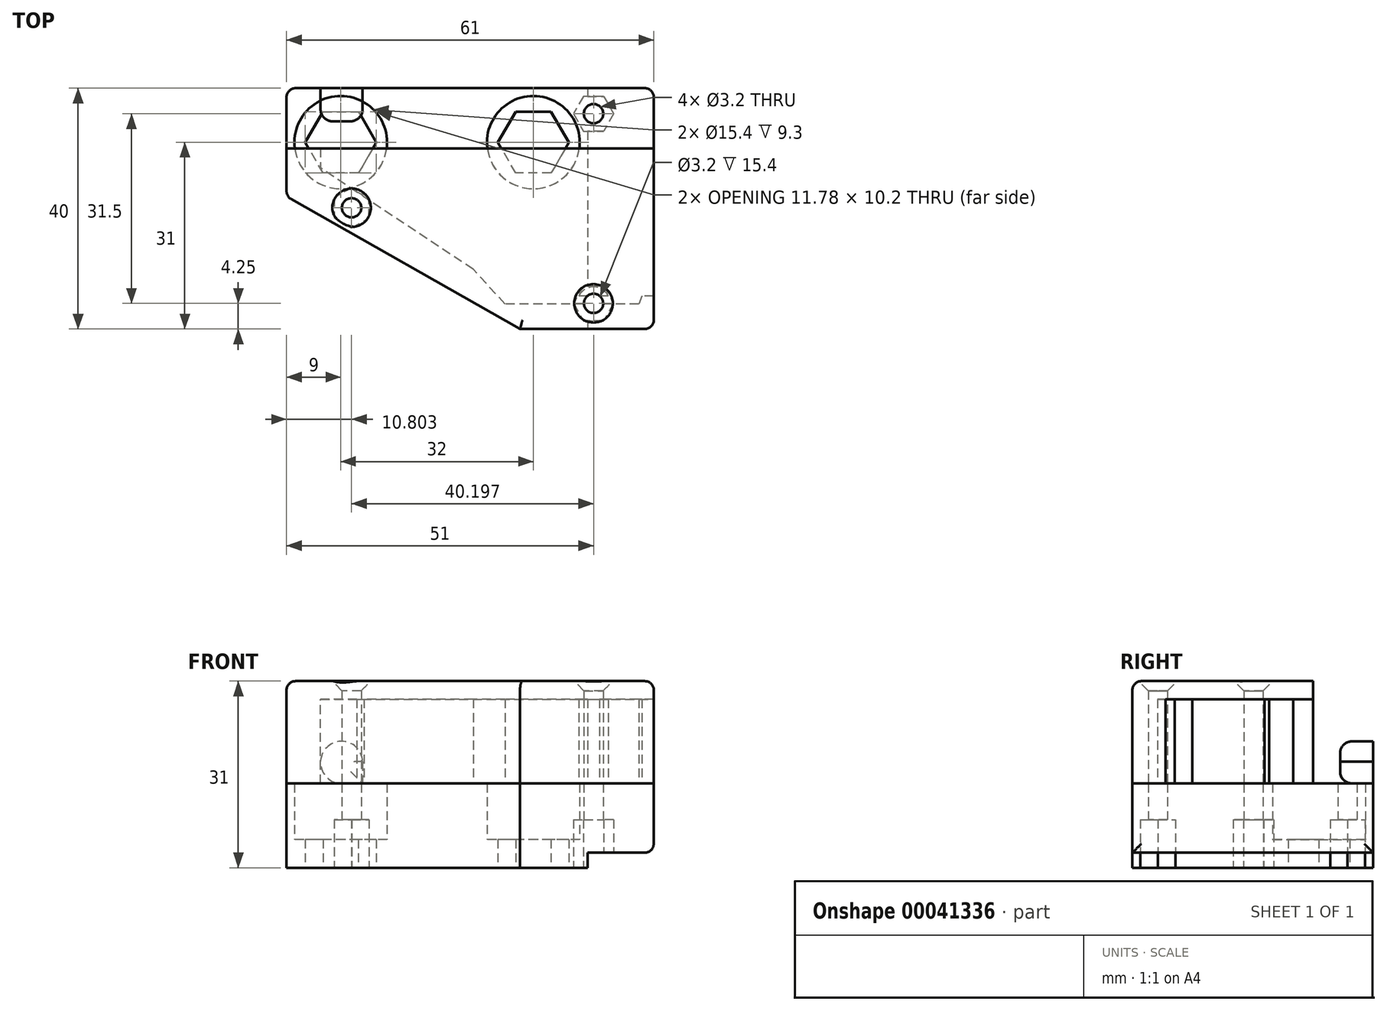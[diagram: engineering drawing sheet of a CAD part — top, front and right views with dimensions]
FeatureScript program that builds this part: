
annotation { "Feature Type Name" : "Feature", "Feature Type Description" : "" }
export const myFeature = defineFeature(function(context is Context, id is Id, definition is map)
    precondition{}
    {
        {
            var Q0;
            Q0=qCreatedBy(makeId("Top.planeOp"),FACE);
            var sketch = newSketch(context, id + "F0", { "sketchPlane" : qUnion([Q0])});
            skLineSegment(sketch, "E0", {"start": v(0, 0) * mm, "end": v(16, 0) * mm, "construction": true});
            skLineSegment(sketch, "E1", {"start": v(0, 0) * mm, "end": v(-16, 0) * mm, "construction": true});
            skCircle(sketch, "E2.cCircle", {"center": v(-16, 0) * mm, "radius": 5.1 * mm, "construction": true});
            skLineSegment(sketch, "E2.0", {"start": v(-13.06, -5.1) * mm, "end": v(-18.94, -5.1) * mm});
            skLineSegment(sketch, "E2.1", {"start": v(-18.94, -5.1) * mm, "end": v(-21.89, 0) * mm});
            skLineSegment(sketch, "E2.2", {"start": v(-21.89, 0) * mm, "end": v(-18.94, 5.1) * mm});
            skLineSegment(sketch, "E2.3", {"start": v(-18.94, 5.1) * mm, "end": v(-13.06, 5.1) * mm});
            skLineSegment(sketch, "E2.4", {"start": v(-13.06, 5.1) * mm, "end": v(-10.11, 0) * mm});
            skLineSegment(sketch, "E2.5", {"start": v(-10.11, 0) * mm, "end": v(-13.06, -5.1) * mm});
            skPoint(sketch, "E2.0.midPoint", {"position": v(-16, -5.1) * mm});
            skCircle(sketch, "E3.cCircle", {"center": v(16, 0) * mm, "radius": 5.1 * mm, "construction": true});
            skLineSegment(sketch, "E3.0", {"start": v(18.94, -5.1) * mm, "end": v(13.06, -5.1) * mm});
            skLineSegment(sketch, "E3.1", {"start": v(13.06, -5.1) * mm, "end": v(10.11, 0) * mm});
            skLineSegment(sketch, "E3.2", {"start": v(10.11, 0) * mm, "end": v(13.06, 5.1) * mm});
            skLineSegment(sketch, "E3.3", {"start": v(13.06, 5.1) * mm, "end": v(18.94, 5.1) * mm});
            skLineSegment(sketch, "E3.4", {"start": v(18.94, 5.1) * mm, "end": v(21.89, 0) * mm});
            skLineSegment(sketch, "E3.5", {"start": v(21.89, 0) * mm, "end": v(18.94, -5.1) * mm});
            skPoint(sketch, "E3.0.midPoint", {"position": v(16, -5.1) * mm});
            skLineSegment(sketch, "E4.rect.bottom", {"start": v(25, 9) * mm, "end": v(-25, 9) * mm});
            skLineSegment(sketch, "E4.rect.top", {"start": v(25, -9) * mm, "end": v(-25, -9) * mm});
            skLineSegment(sketch, "E4.rect.left", {"start": v(25, 9) * mm, "end": v(25, -9) * mm});
            skLineSegment(sketch, "E4.rect.right", {"start": v(-25, 9) * mm, "end": v(-25, -9) * mm});
            skPoint(sketch, "E4.rect.middle", {"position": v(0, 0) * mm});
            skCircle(sketch, "E5", {"center": v(16, 0) * mm, "radius": 7.7 * mm});
            skCircle(sketch, "E6", {"center": v(-16, 0) * mm, "radius": 7.7 * mm});
            skLineSegment(sketch, "E7", {"start": v(25, -9) * mm, "end": v(25, -31) * mm});
            skLineSegment(sketch, "E8", {"start": v(25, -31) * mm, "end": v(13.8, -31) * mm});
            skLineSegment(sketch, "E9", {"start": v(13.8, -31) * mm, "end": v(-25, -9) * mm});
            skSolve(sketch);
        }
        {
            var Q0;
            Q0=makeQuery(id+"F0.imprint","IMPRINT",FACE,{"disambiguationData":[TD([[makeQuery(id+"F0.imprint","IMPRINT",EDGE,{"derivedFrom":sQuery(id+"F0.wireOp",EDGE,"E2.0")}),1.0]])]});
            var Q1;
            Q1=makeQuery(id+"F0.imprint","IMPRINT",FACE,{"disambiguationData":[TD([[makeQuery(id+"F0.imprint","IMPRINT",EDGE,{"derivedFrom":sQuery(id+"F0.wireOp",EDGE,"E4.rect.bottom")}),1.0]])]});
            var Q2;
            Q2=makeQuery(id+"F0.imprint","IMPRINT",FACE,{"disambiguationData":[TD([[makeQuery(id+"F0.imprint","IMPRINT",EDGE,{"derivedFrom":sQuery(id+"F0.wireOp",EDGE,"E3.0")}),1.0]])]});
            var Q3;
            Q3=makeQuery(id+"F0.imprint","IMPRINT",FACE,{"disambiguationData":[TD([[makeQuery(id+"F0.imprint","IMPRINT",EDGE,{"derivedFrom":sQuery(id+"F0.wireOp",EDGE,"E4.rect.top")}),1.0]])]});
            var Q4;
            Q4=makeQuery(id+"F0.imprint","IMPRINT",FACE,{"disambiguationData":[TD([[makeQuery(id+"F0.imprint","IMPRINT",EDGE,{"derivedFrom":sQuery(id+"F0.wireOp",EDGE,"9e964b0c-50f7-469d-a5f6-e5326cfa843e")}),-1.0]])]});
            var Q5;
            {var subQ3=sQuery(id+"F0.wireOp",EDGE,"6a1c6b45-991d-430d-b84b-9ebeff1134ff.2");Q5=makeQuery(id+"F0.imprint","IMPRINT",FACE,{"disambiguationData":[TD([[makeQuery(id+"F0.imprint","IMPRINT",EDGE,{"derivedFrom":subQ3}),-1.0]])]});}
            var Q6;
            Q6=makeQuery(id+"F0.imprint","IMPRINT",FACE,{"disambiguationData":[TD([[makeQuery(id+"F0.imprint","IMPRINT",EDGE,{"derivedFrom":sQuery(id+"F0.wireOp",EDGE,"208a588a-a936-4bbe-a4cd-ee4cf070bca5.5")}),-1.0]])]});
            var Q7;
            {var subQ3=sQuery(id+"F0.wireOp",EDGE,"6a1c6b45-991d-430d-b84b-9ebeff1134ff.4");Q7=makeQuery(id+"F0.imprint","IMPRINT",FACE,{"disambiguationData":[TD([[makeQuery(id+"F0.imprint","IMPRINT",EDGE,{"derivedFrom":subQ3}),-1.0]])]});}
            var Q8;
            {var subQ1=sQuery(id+"F0.wireOp",EDGE,"E4.rect.top");var subQ3=sQuery(id+"F0.wireOp",EDGE,"5dbff245-9a07-4e52-9307-8249a6cdc635.0");var subQ5=makeQuery(id+"F0.imprint","INTERSECT",VERTEX,{"derivedFrom":[subQ1,subQ3]});Q8=makeQuery(id+"F0.imprint","IMPRINT",FACE,{"disambiguationData":[TD([[makeQuery(id+"F0.imprint","IMPRINT",EDGE,{"disambiguationData":[TD([[subQ5,-1.0]])],"derivedFrom":subQ1}),-1.0]])]});}
            extrude(context, id + "F1", {"entities" : qUnion([Q0, Q1, Q2, Q3, Q4, Q5, Q6, Q7, Q8]), "depth" : 4.7 * mm});
        }
        {
            var Q0;
            Q0 = qSketchRegion(id + "F0", true);
            var Q1;
            {var subQ4=sQuery(id+"F0.wireOp",EDGE,"6a1c6b45-991d-430d-b84b-9ebeff1134ff.2");Q1=makeQuery(id+"F0.imprint","IMPRINT",FACE,{"disambiguationData":[TD([[makeQuery(id+"F0.imprint","IMPRINT",EDGE,{"derivedFrom":subQ4}),-1.0]])]});}
            var Q2;
            Q2=makeQuery(id+"F0.imprint","IMPRINT",FACE,{"disambiguationData":[TD([[makeQuery(id+"F0.imprint","IMPRINT",EDGE,{"derivedFrom":sQuery(id+"F0.wireOp",EDGE,"9e964b0c-50f7-469d-a5f6-e5326cfa843e")}),-1.0]])]});
            var Q3;
            Q3=makeQuery(id+"F0.imprint","IMPRINT",FACE,{"disambiguationData":[TD([[makeQuery(id+"F0.imprint","IMPRINT",EDGE,{"derivedFrom":sQuery(id+"F0.wireOp",EDGE,"208a588a-a936-4bbe-a4cd-ee4cf070bca5.5")}),-1.0]])]});
            extrude(context, id + "F2", {"entities" : qUnion([Q0, Q1, Q2, Q3]), "operationType" : NewBodyOperationType.ADD, "depth" : 14 * mm});
        }
        {
            var Q0;
            Q0=qCreatedBy(makeId("Top.planeOp"),FACE);
            cPlane(context, id + "F3", {"entities" : qUnion([Q0]), "cplaneType" : CPlaneType.OFFSET, "offset" : 2.5 * mm, "width" : 150 * mm, "height" : 150 * mm});
        }
        {
            var Q0;
            Q0=qCreatedBy(id+"F3.planeOp",FACE);
            var sketch = newSketch(context, id + "F4", { "sketchPlane" : qUnion([Q0])});
            skLineSegment(sketch, "E10.bottom", {"start": v(25, 9) * mm, "end": v(36, 9) * mm});
            skLineSegment(sketch, "E10.top", {"start": v(25, -31) * mm, "end": v(36, -31) * mm});
            skLineSegment(sketch, "E10.left", {"start": v(25, 9) * mm, "end": v(25, -31) * mm});
            skLineSegment(sketch, "E10.right", {"start": v(36, 9) * mm, "end": v(36, -31) * mm});
            skCircle(sketch, "E11.0", {"center": v(16, 0) * mm, "radius": 7.7 * mm});
            skSolve(sketch);
        }
        {
            var Q0;
            Q0=makeQuery(id+"F4.imprint","IMPRINT",FACE,{"disambiguationData":[TD([[makeQuery(id+"F4.imprint","IMPRINT",EDGE,{"derivedFrom":sQuery(id+"F4.wireOp",EDGE,"E10.bottom")}),-1.0]])]});
            var Q1;
            Q1=makeQuery(id+"F2.opExtrude","CAP_FACE",FACE,{"disambiguationData":[OSD([sQuery(id+"F0.wireOp",EDGE,"E4.rect.bottom"),sQuery(id+"F0.wireOp",EDGE,"E4.rect.left"),sQuery(id+"F0.wireOp",EDGE,"E4.rect.right"),sQuery(id+"F0.wireOp",EDGE,"E5"),sQuery(id+"F0.wireOp",EDGE,"E6"),sQuery(id+"F0.wireOp",EDGE,"E7"),sQuery(id+"F0.wireOp",EDGE,"ee43d7b4-246c-4edb-8c6c-6255f297e4f2")])],"isStart":false});
            extrude(context, id + "F5", {"entities" : qUnion([Q0]), "operationType" : NewBodyOperationType.ADD, "endBound" : BoundingType.UP_TO_SURFACE, "endBoundEntityFace" : qUnion([Q1]), "depth" : 25 * mm});
        }
        {
            var Q0;
            Q0=makeQuery(id+"F5.boolean.opBoolean","MERGE",FACE,{"derivedFrom":[makeQuery(id+"F2.opExtrude","CAP_FACE",FACE,{"disambiguationData":[OSD([sQuery(id+"F0.wireOp",EDGE,"E4.rect.bottom"),sQuery(id+"F0.wireOp",EDGE,"E4.rect.left"),sQuery(id+"F0.wireOp",EDGE,"E4.rect.right"),sQuery(id+"F0.wireOp",EDGE,"E5"),sQuery(id+"F0.wireOp",EDGE,"E6"),sQuery(id+"F0.wireOp",EDGE,"E7"),sQuery(id+"F0.wireOp",EDGE,"ee43d7b4-246c-4edb-8c6c-6255f297e4f2")])],"isStart":false}),makeQuery(id+"F5.opExtrude","CAP_FACE",FACE,{"disambiguationData":[OSD([sQuery(id+"F4.wireOp",EDGE,"E10.bottom"),sQuery(id+"F4.wireOp",EDGE,"E10.top"),sQuery(id+"F4.wireOp",EDGE,"E10.left"),sQuery(id+"F4.wireOp",EDGE,"E10.right")])],"isStart":false})]});
            var sketch = newSketch(context, id + "F6", { "sketchPlane" : qUnion([Q0])});
            skSolve(sketch);
        }
        {
            var Q0;
            {var subQ10=sQuery(id+"F6.wireOp",EDGE,"a482f5d8-160b-4c89-b4e5-af63eeadc495.top");Q0=makeQuery(id+"F6.imprint","IMPRINT",FACE,{"disambiguationData":[TD([[makeQuery(id+"F6.imprint","IMPRINT",EDGE,{"derivedFrom":subQ10}),1.0]])]});}
            var Q1;
            Q1=makeQuery(id+"F6.imprint","IMPRINT",FACE,{"disambiguationData":[TD([[makeQuery(id+"F6.imprint","IMPRINT",EDGE,{"derivedFrom":makeQuery(id+"F2.opExtrude","CAP_EDGE",EDGE,{"disambiguationData":[OSD([sQuery(id+"F0.wireOp",EDGE,"E6")])],"isStart":false})}),1.0]])]});
            var Q2;
            {var subQ0=sQuery(id+"F6.wireOp",EDGE,"a482f5d8-160b-4c89-b4e5-af63eeadc495.right");var subQ3=sQuery(id+"F6.wireOp",EDGE,"a482f5d8-160b-4c89-b4e5-af63eeadc495.bottom");var subQ4=makeQuery(id+"F6.imprint","INTERSECT",VERTEX,{"derivedFrom":[subQ3,subQ0]});Q2=makeQuery(id+"F6.imprint","IMPRINT",FACE,{"disambiguationData":[TD([[makeQuery(id+"F6.imprint","IMPRINT",EDGE,{"disambiguationData":[TD([[subQ4,1.0]])],"derivedFrom":subQ3}),-1.0]])]});}
            var Q3;
            {var subQ1=sQuery(id+"F6.wireOp",EDGE,"a482f5d8-160b-4c89-b4e5-af63eeadc495.right");var subQ3=sQuery(id+"F6.wireOp",EDGE,"a482f5d8-160b-4c89-b4e5-af63eeadc495.bottom");var subQ5=makeQuery(id+"F6.imprint","INTERSECT",VERTEX,{"derivedFrom":[subQ3,subQ1]});Q3=makeQuery(id+"F6.imprint","IMPRINT",FACE,{"disambiguationData":[TD([[makeQuery(id+"F6.imprint","IMPRINT",EDGE,{"disambiguationData":[TD([[subQ5,1.0]])],"derivedFrom":subQ3}),1.0]])]});}
            var Q4;
            Q4=makeQuery(id+"F6.imprint","IMPRINT",FACE,{"disambiguationData":[TD([[makeQuery(id+"F6.imprint","IMPRINT",EDGE,{"derivedFrom":makeQuery(id+"F2.opExtrude","CAP_EDGE",EDGE,{"disambiguationData":[OSD([sQuery(id+"F0.wireOp",EDGE,"E4.rect.right")])],"isStart":false})}),1.0]])]});
            var Q5;
            Q5=makeQuery(id+"F6.imprint","IMPRINT",FACE,{"disambiguationData":[TD([[makeQuery(id+"F6.imprint","IMPRINT",EDGE,{"derivedFrom":makeQuery(id+"F2.opExtrude","CAP_EDGE",EDGE,{"disambiguationData":[OSD([sQuery(id+"F0.wireOp",EDGE,"E5")])],"isStart":false})}),1.0]])]});
            extrude(context, id + "F7", {"entities" : qUnion([Q0, Q1, Q2, Q3, Q4, Q5]), "depth" : 17 * mm});
        }
        {
            var Q0;
            Q0=makeQuery(id+"F7.opExtrude","CAP_FACE",FACE,{"disambiguationData":[OSD([sQuery(id+"F0.wireOp",EDGE,"E4.rect.bottom"),sQuery(id+"F0.wireOp",EDGE,"E4.rect.right"),sQuery(id+"F0.wireOp",EDGE,"E8"),sQuery(id+"F0.wireOp",EDGE,"E9"),sQuery(id+"F4.wireOp",EDGE,"E10.bottom"),sQuery(id+"F4.wireOp",EDGE,"E10.top"),sQuery(id+"F4.wireOp",EDGE,"E10.right")])],"isStart":true});
            var sketch = newSketch(context, id + "F8", { "sketchPlane" : qUnion([Q0])});
            skLineSegment(sketch, "E12.bottom", {"start": v(36, -3.5) * mm, "end": v(6, -3.5) * mm});
            skLineSegment(sketch, "E12.top", {"start": v(36, 25.5) * mm, "end": v(6, 25.5) * mm});
            skLineSegment(sketch, "E12.left", {"start": v(36, -3.5) * mm, "end": v(36, 25.5) * mm});
            skLineSegment(sketch, "E12.right", {"start": v(6, -3.5) * mm, "end": v(6, 25.5) * mm});
            skLineSegment(sketch, "E13", {"start": v(6, 21.06) * mm, "end": v(-19.35, 4.28) * mm});
            skLineSegment(sketch, "E14", {"start": v(6, -3.5) * mm, "end": v(-19.35, -3.5) * mm});
            skLineSegment(sketch, "E15", {"start": v(34, 25.5) * mm, "end": v(33.53, 26.85) * mm});
            skLineSegment(sketch, "E16", {"start": v(33.53, 26.85) * mm, "end": v(11.28, 26.85) * mm});
            skLineSegment(sketch, "E17", {"start": v(11.28, 26.85) * mm, "end": v(6, 21.06) * mm});
            skLineSegment(sketch, "E18", {"start": v(34, -3.5) * mm, "end": v(33.65, -5.03) * mm});
            skLineSegment(sketch, "E19", {"start": v(33.65, -5.03) * mm, "end": v(6.15, -5.03) * mm});
            skLineSegment(sketch, "E20", {"start": v(6, -3.5) * mm, "end": v(6.15, -5.03) * mm});
            skCircle(sketch, "E21", {"center": v(26, 26.75) * mm, "radius": 2.75 * mm});
            skCircle(sketch, "E22", {"center": v(26, 26.75) * mm, "radius": 1.6 * mm});
            skCircle(sketch, "E23", {"center": v(26, -4.75) * mm, "radius": 2.75 * mm});
            skCircle(sketch, "E24", {"center": v(26, -4.75) * mm, "radius": 1.6 * mm});
            skCircle(sketch, "E25", {"center": v(-14.2, 10.88) * mm, "radius": 2.75 * mm});
            skCircle(sketch, "E26", {"center": v(-14.2, 10.88) * mm, "radius": 1.6 * mm});
            skLineSegment(sketch, "E27", {"start": v(-19.35, -3.5) * mm, "end": v(-19.35, 4.28) * mm});
            skSolve(sketch);
        }
        {
            var Q0;
            {var subQ5=sQuery(id+"F8.wireOp",EDGE,"E14");Q0=makeQuery(id+"F8.imprint","IMPRINT",FACE,{"disambiguationData":[TD([[makeQuery(id+"F8.imprint","IMPRINT",EDGE,{"derivedFrom":subQ5}),-1.0]])]});}
            var Q1;
            {var subQ9=sQuery(id+"F8.wireOp",EDGE,"E12.left");Q1=makeQuery(id+"F8.imprint","IMPRINT",FACE,{"disambiguationData":[TD([[makeQuery(id+"F8.imprint","IMPRINT",EDGE,{"derivedFrom":subQ9}),1.0]])]});}
            var Q2;
            {var subQ0=sQuery(id+"F8.wireOp",EDGE,"E21");var subQ3=sQuery(id+"F8.wireOp",EDGE,"E12.top");var subQ4=makeQuery(id+"F8.imprint","INTERSECT",VERTEX,{"disambiguationData":[OD(1.0)],"derivedFrom":[subQ3,subQ0]});Q2=makeQuery(id+"F8.imprint","IMPRINT",FACE,{"disambiguationData":[TD([[makeQuery(id+"F8.imprint","IMPRINT",EDGE,{"disambiguationData":[TD([[subQ4,-1.0]])],"derivedFrom":subQ3}),-1.0]])]});}
            var Q3;
            {var subQ0=sQuery(id+"F8.wireOp",EDGE,"E22");var subQ3=sQuery(id+"F8.wireOp",EDGE,"E12.top");var subQ4=makeQuery(id+"F8.imprint","INTERSECT",VERTEX,{"disambiguationData":[OD(0.0)],"derivedFrom":[subQ3,subQ0]});Q3=makeQuery(id+"F8.imprint","IMPRINT",FACE,{"disambiguationData":[TD([[makeQuery(id+"F8.imprint","IMPRINT",EDGE,{"disambiguationData":[TD([[subQ4,-1.0]])],"derivedFrom":subQ3}),-1.0]])]});}
            var Q4;
            {var subQ5=sQuery(id+"F8.wireOp",EDGE,"E15");Q4=makeQuery(id+"F8.imprint","IMPRINT",FACE,{"disambiguationData":[TD([[makeQuery(id+"F8.imprint","IMPRINT",EDGE,{"derivedFrom":subQ5}),1.0]])]});}
            var Q5;
            {var subQ3=sQuery(id+"F8.wireOp",EDGE,"E12.top");var subQ5=sQuery(id+"F8.wireOp",EDGE,"E22");var subQ7=makeQuery(id+"F8.imprint","INTERSECT",VERTEX,{"disambiguationData":[OD(1.0)],"derivedFrom":[subQ3,subQ5]});Q5=makeQuery(id+"F8.imprint","IMPRINT",FACE,{"disambiguationData":[TD([[makeQuery(id+"F8.imprint","IMPRINT",EDGE,{"disambiguationData":[TD([[subQ7,-1.0]])],"derivedFrom":subQ3}),-1.0]])]});}
            var Q6;
            {var subQ0=sQuery(id+"F8.wireOp",EDGE,"E21");var subQ3=sQuery(id+"F8.wireOp",EDGE,"E12.top");var subQ4=makeQuery(id+"F8.imprint","INTERSECT",VERTEX,{"disambiguationData":[OD(0.0)],"derivedFrom":[subQ3,subQ0]});Q6=makeQuery(id+"F8.imprint","IMPRINT",FACE,{"disambiguationData":[TD([[makeQuery(id+"F8.imprint","IMPRINT",EDGE,{"disambiguationData":[TD([[subQ4,-1.0]])],"derivedFrom":subQ3}),-1.0]])]});}
            var Q7;
            {var subQ1=sQuery(id+"F8.wireOp",EDGE,"E12.top");var subQ4=sQuery(id+"F8.wireOp",EDGE,"E21");var subQ6=makeQuery(id+"F8.imprint","INTERSECT",VERTEX,{"disambiguationData":[OD(0.0)],"derivedFrom":[subQ1,subQ4]});Q7=makeQuery(id+"F8.imprint","IMPRINT",FACE,{"disambiguationData":[TD([[makeQuery(id+"F8.imprint","IMPRINT",EDGE,{"disambiguationData":[TD([[subQ6,-1.0]])],"derivedFrom":subQ1}),1.0]])]});}
            var Q8;
            {var subQ0=sQuery(id+"F8.wireOp",EDGE,"E22");var subQ1=sQuery(id+"F8.wireOp",EDGE,"E12.top");var subQ3=makeQuery(id+"F8.imprint","INTERSECT",VERTEX,{"disambiguationData":[OD(0.0)],"derivedFrom":[subQ1,subQ0]});Q8=makeQuery(id+"F8.imprint","IMPRINT",FACE,{"disambiguationData":[TD([[makeQuery(id+"F8.imprint","IMPRINT",EDGE,{"disambiguationData":[TD([[subQ3,-1.0]])],"derivedFrom":subQ1}),1.0]])]});}
            var Q9;
            {var subQ0=sQuery(id+"F8.wireOp",EDGE,"E23");var subQ3=sQuery(id+"F8.wireOp",EDGE,"E12.bottom");var subQ4=makeQuery(id+"F8.imprint","INTERSECT",VERTEX,{"disambiguationData":[OD(0.0)],"derivedFrom":[subQ3,subQ0]});Q9=makeQuery(id+"F8.imprint","IMPRINT",FACE,{"disambiguationData":[TD([[makeQuery(id+"F8.imprint","IMPRINT",EDGE,{"disambiguationData":[TD([[subQ4,-1.0]])],"derivedFrom":subQ3}),1.0]])]});}
            var Q10;
            {var subQ3=sQuery(id+"F8.wireOp",EDGE,"E18");Q10=makeQuery(id+"F8.imprint","IMPRINT",FACE,{"disambiguationData":[TD([[makeQuery(id+"F8.imprint","IMPRINT",EDGE,{"derivedFrom":subQ3}),-1.0]])]});}
            var Q11;
            {var subQ3=sQuery(id+"F8.wireOp",EDGE,"E12.bottom");var subQ5=sQuery(id+"F8.wireOp",EDGE,"E24");var subQ7=makeQuery(id+"F8.imprint","INTERSECT",VERTEX,{"disambiguationData":[OD(1.0)],"derivedFrom":[subQ3,subQ5]});Q11=makeQuery(id+"F8.imprint","IMPRINT",FACE,{"disambiguationData":[TD([[makeQuery(id+"F8.imprint","IMPRINT",EDGE,{"disambiguationData":[TD([[subQ7,-1.0]])],"derivedFrom":subQ3}),1.0]])]});}
            var Q12;
            {var subQ5=sQuery(id+"F8.wireOp",EDGE,"E20");Q12=makeQuery(id+"F8.imprint","IMPRINT",FACE,{"disambiguationData":[TD([[makeQuery(id+"F8.imprint","IMPRINT",EDGE,{"derivedFrom":subQ5}),1.0]])]});}
            var Q13;
            {var subQ1=sQuery(id+"F8.wireOp",EDGE,"E12.bottom");var subQ4=sQuery(id+"F8.wireOp",EDGE,"E23");var subQ6=makeQuery(id+"F8.imprint","INTERSECT",VERTEX,{"disambiguationData":[OD(0.0)],"derivedFrom":[subQ1,subQ4]});Q13=makeQuery(id+"F8.imprint","IMPRINT",FACE,{"disambiguationData":[TD([[makeQuery(id+"F8.imprint","IMPRINT",EDGE,{"disambiguationData":[TD([[subQ6,-1.0]])],"derivedFrom":subQ1}),-1.0]])]});}
            var Q14;
            {var subQ0=sQuery(id+"F8.wireOp",EDGE,"E24");var subQ1=sQuery(id+"F8.wireOp",EDGE,"E12.bottom");var subQ3=makeQuery(id+"F8.imprint","INTERSECT",VERTEX,{"disambiguationData":[OD(0.0)],"derivedFrom":[subQ1,subQ0]});Q14=makeQuery(id+"F8.imprint","IMPRINT",FACE,{"disambiguationData":[TD([[makeQuery(id+"F8.imprint","IMPRINT",EDGE,{"disambiguationData":[TD([[subQ3,-1.0]])],"derivedFrom":subQ1}),-1.0]])]});}
            var Q15;
            {var subQ0=sQuery(id+"F8.wireOp",EDGE,"E24");var subQ3=sQuery(id+"F8.wireOp",EDGE,"E12.bottom");var subQ4=makeQuery(id+"F8.imprint","INTERSECT",VERTEX,{"disambiguationData":[OD(0.0)],"derivedFrom":[subQ3,subQ0]});Q15=makeQuery(id+"F8.imprint","IMPRINT",FACE,{"disambiguationData":[TD([[makeQuery(id+"F8.imprint","IMPRINT",EDGE,{"disambiguationData":[TD([[subQ4,-1.0]])],"derivedFrom":subQ3}),1.0]])]});}
            extrude(context, id + "F9", {"entities" : qUnion([Q0, Q1, Q2, Q3, Q4, Q5, Q6, Q7, Q8, Q9, Q10, Q11, Q12, Q13, Q14, Q15]), "operationType" : NewBodyOperationType.REMOVE, "oppositeDirection" : true, "depth" : 14 * mm});
        }
        {
            var Q0;
            Q0=makeQuery(id+"F8.imprint","IMPRINT",FACE,{"disambiguationData":[TD([[makeQuery(id+"F8.imprint","IMPRINT",EDGE,{"derivedFrom":sQuery(id+"F8.wireOp",EDGE,"E26")}),1.0]])]});
            var Q1;
            {var subQ0=sQuery(id+"F8.wireOp",EDGE,"E24");var subQ1=sQuery(id+"F8.wireOp",EDGE,"E19");var subQ3=makeQuery(id+"F8.imprint","INTERSECT",VERTEX,{"disambiguationData":[OD(0.0)],"derivedFrom":[subQ1,subQ0]});Q1=makeQuery(id+"F8.imprint","IMPRINT",FACE,{"disambiguationData":[TD([[makeQuery(id+"F8.imprint","IMPRINT",EDGE,{"disambiguationData":[TD([[subQ3,-1.0]])],"derivedFrom":subQ1}),1.0]])]});}
            var Q2;
            {var subQ0=sQuery(id+"F8.wireOp",EDGE,"E24");var subQ1=sQuery(id+"F8.wireOp",EDGE,"E19");var subQ3=makeQuery(id+"F8.imprint","INTERSECT",VERTEX,{"disambiguationData":[OD(0.0)],"derivedFrom":[subQ1,subQ0]});Q2=makeQuery(id+"F8.imprint","IMPRINT",FACE,{"disambiguationData":[TD([[makeQuery(id+"F8.imprint","IMPRINT",EDGE,{"disambiguationData":[TD([[subQ3,-1.0]])],"derivedFrom":subQ1}),-1.0]])]});}
            var Q3;
            {var subQ0=sQuery(id+"F8.wireOp",EDGE,"E22");var subQ1=sQuery(id+"F8.wireOp",EDGE,"E16");var subQ3=makeQuery(id+"F8.imprint","INTERSECT",VERTEX,{"disambiguationData":[OD(0.0)],"derivedFrom":[subQ1,subQ0]});Q3=makeQuery(id+"F8.imprint","IMPRINT",FACE,{"disambiguationData":[TD([[makeQuery(id+"F8.imprint","IMPRINT",EDGE,{"disambiguationData":[TD([[subQ3,-1.0]])],"derivedFrom":subQ1}),-1.0]])]});}
            var Q4;
            {var subQ0=sQuery(id+"F8.wireOp",EDGE,"E22");var subQ1=sQuery(id+"F8.wireOp",EDGE,"E16");var subQ3=makeQuery(id+"F8.imprint","INTERSECT",VERTEX,{"disambiguationData":[OD(0.0)],"derivedFrom":[subQ1,subQ0]});Q4=makeQuery(id+"F8.imprint","IMPRINT",FACE,{"disambiguationData":[TD([[makeQuery(id+"F8.imprint","IMPRINT",EDGE,{"disambiguationData":[TD([[subQ3,-1.0]])],"derivedFrom":subQ1}),1.0]])]});}
            var Q5;
            {var subQ0=sQuery(id+"F8.wireOp",EDGE,"E24");var subQ1=sQuery(id+"F8.wireOp",EDGE,"E12.bottom");var subQ3=makeQuery(id+"F8.imprint","INTERSECT",VERTEX,{"disambiguationData":[OD(0.0)],"derivedFrom":[subQ1,subQ0]});Q5=makeQuery(id+"F8.imprint","IMPRINT",FACE,{"disambiguationData":[TD([[makeQuery(id+"F8.imprint","IMPRINT",EDGE,{"disambiguationData":[TD([[subQ3,-1.0]])],"derivedFrom":subQ1}),-1.0]])]});}
            var Q6;
            {var subQ0=sQuery(id+"F8.wireOp",EDGE,"E22");var subQ1=sQuery(id+"F8.wireOp",EDGE,"E12.top");var subQ3=makeQuery(id+"F8.imprint","INTERSECT",VERTEX,{"disambiguationData":[OD(0.0)],"derivedFrom":[subQ1,subQ0]});Q6=makeQuery(id+"F8.imprint","IMPRINT",FACE,{"disambiguationData":[TD([[makeQuery(id+"F8.imprint","IMPRINT",EDGE,{"disambiguationData":[TD([[subQ3,-1.0]])],"derivedFrom":subQ1}),1.0]])]});}
            extrude(context, id + "F10", {"entities" : qUnion([Q0, Q1, Q2, Q3, Q4, Q5, Q6]), "operationType" : NewBodyOperationType.REMOVE, "endBound" : BoundingType.SYMMETRIC, "oppositeDirection" : true, "depth" : 50 * mm});
        }
        {
            var Q0;
            Q0=makeQuery(id+"F7.opExtrude","CAP_FACE",FACE,{"disambiguationData":[OSD([sQuery(id+"F0.wireOp",EDGE,"E4.rect.bottom"),sQuery(id+"F0.wireOp",EDGE,"E4.rect.right"),sQuery(id+"F0.wireOp",EDGE,"E8"),sQuery(id+"F0.wireOp",EDGE,"E9"),sQuery(id+"F4.wireOp",EDGE,"E10.bottom"),sQuery(id+"F4.wireOp",EDGE,"E10.top"),sQuery(id+"F4.wireOp",EDGE,"E10.right")])],"isStart":false});
            var sketch = newSketch(context, id + "F11", { "sketchPlane" : qUnion([Q0])});
            skPoint(sketch, "E28", {"position": v(-14.2, -10.88) * mm});
            skPoint(sketch, "E29", {"position": v(26, -26.75) * mm});
            skPoint(sketch, "E30", {"position": v(26, 4.75) * mm});
            skSolve(sketch);
        }
        {
            var Q0;
            Q0=sQuery(id+"F11.wireOp",VERTEX,"E30");
            var Q1;
            Q1=sQuery(id+"F11.wireOp",VERTEX,"E29");
            var Q2;
            Q2=sQuery(id+"F11.wireOp",VERTEX,"E28");
            var Q3;
            Q3=makeQuery(id+"F7.opExtrude","SWEPT_BODY",BODY,{"disambiguationData":[OSD([sQuery(id+"F0.wireOp",EDGE,"E4.rect.bottom"),sQuery(id+"F0.wireOp",EDGE,"E4.rect.right"),sQuery(id+"F0.wireOp",EDGE,"E8"),sQuery(id+"F0.wireOp",EDGE,"E9"),sQuery(id+"F4.wireOp",EDGE,"E10.bottom"),sQuery(id+"F4.wireOp",EDGE,"E10.top"),sQuery(id+"F4.wireOp",EDGE,"E10.right")])]});
            hole(context, id + "F12", {"style" : HoleStyle.C_SINK, "holeDiameter" : 3.2 * mm, "cSinkDiameter" : 6.4 * mm, "endStyle" : HoleEndStyle.THROUGH, "locations" : qUnion([Q0, Q1, Q2]), "scope" : qUnion([Q3]), "cSinkAngle" : 90 * degree});
        }
        {
            var Q0;
            Q0=makeQuery(id+"F1.opExtrude","CAP_FACE",FACE,{"disambiguationData":[OSD([sQuery(id+"F0.wireOp",EDGE,"E2.0"),sQuery(id+"F0.wireOp",EDGE,"E2.1"),sQuery(id+"F0.wireOp",EDGE,"E2.2"),sQuery(id+"F0.wireOp",EDGE,"E2.3"),sQuery(id+"F0.wireOp",EDGE,"E2.4"),sQuery(id+"F0.wireOp",EDGE,"E2.5"),sQuery(id+"F0.wireOp",EDGE,"E3.0"),sQuery(id+"F0.wireOp",EDGE,"E3.1"),sQuery(id+"F0.wireOp",EDGE,"E3.2"),sQuery(id+"F0.wireOp",EDGE,"E3.3"),sQuery(id+"F0.wireOp",EDGE,"E3.4"),sQuery(id+"F0.wireOp",EDGE,"E3.5"),sQuery(id+"F0.wireOp",EDGE,"E4.rect.bottom"),sQuery(id+"F0.wireOp",EDGE,"E4.rect.left"),sQuery(id+"F0.wireOp",EDGE,"E4.rect.right"),sQuery(id+"F0.wireOp",EDGE,"E7"),sQuery(id+"F0.wireOp",EDGE,"E8"),sQuery(id+"F0.wireOp",EDGE,"E9")])],"isStart":true});
            var sketch = newSketch(context, id + "F13", { "sketchPlane" : qUnion([Q0])});
            skCircle(sketch, "E31.0", {"center": v(-14.2, 10.88) * mm, "radius": 1.6 * mm});
            skCircle(sketch, "E32.0", {"center": v(26, -4.75) * mm, "radius": 1.6 * mm});
            skCircle(sketch, "E33.0", {"center": v(26, 26.75) * mm, "radius": 1.6 * mm});
            skCircle(sketch, "E34.cCircle", {"center": v(-14.2, 10.88) * mm, "radius": 2.9 * mm, "construction": true});
            skLineSegment(sketch, "E34.0", {"start": v(-11.3, 9.21) * mm, "end": v(-14.19, 7.53) * mm});
            skLineSegment(sketch, "E34.1", {"start": v(-14.19, 7.53) * mm, "end": v(-17.1, 9.2) * mm});
            skLineSegment(sketch, "E34.2", {"start": v(-17.1, 9.2) * mm, "end": v(-17.1, 12.54) * mm});
            skLineSegment(sketch, "E34.3", {"start": v(-17.1, 12.54) * mm, "end": v(-14.2, 14.23) * mm});
            skLineSegment(sketch, "E34.4", {"start": v(-14.2, 14.23) * mm, "end": v(-11.3, 12.56) * mm});
            skLineSegment(sketch, "E34.5", {"start": v(-11.3, 12.56) * mm, "end": v(-11.3, 9.21) * mm});
            skPoint(sketch, "E34.0.midPoint", {"position": v(-12.74, 8.37) * mm});
            skCircle(sketch, "E35.cCircle", {"center": v(26, 26.75) * mm, "radius": 2.9 * mm, "construction": true});
            skLineSegment(sketch, "E35.0", {"start": v(27.67, 23.85) * mm, "end": v(24.33, 23.85) * mm});
            skLineSegment(sketch, "E35.1", {"start": v(24.33, 23.85) * mm, "end": v(22.65, 26.75) * mm});
            skLineSegment(sketch, "E35.2", {"start": v(22.65, 26.75) * mm, "end": v(24.33, 29.65) * mm});
            skLineSegment(sketch, "E35.3", {"start": v(24.33, 29.65) * mm, "end": v(27.67, 29.65) * mm});
            skLineSegment(sketch, "E35.4", {"start": v(27.67, 29.65) * mm, "end": v(29.35, 26.75) * mm});
            skLineSegment(sketch, "E35.5", {"start": v(29.35, 26.75) * mm, "end": v(27.67, 23.85) * mm});
            skPoint(sketch, "E35.0.midPoint", {"position": v(26, 23.85) * mm});
            skCircle(sketch, "E36.cCircle", {"center": v(26, -4.75) * mm, "radius": 2.9 * mm, "construction": true});
            skLineSegment(sketch, "E36.0", {"start": v(24.33, -1.85) * mm, "end": v(27.67, -1.85) * mm});
            skLineSegment(sketch, "E36.1", {"start": v(27.67, -1.85) * mm, "end": v(29.35, -4.75) * mm});
            skLineSegment(sketch, "E36.2", {"start": v(29.35, -4.75) * mm, "end": v(27.67, -7.65) * mm});
            skLineSegment(sketch, "E36.3", {"start": v(27.67, -7.65) * mm, "end": v(24.33, -7.65) * mm});
            skLineSegment(sketch, "E36.4", {"start": v(24.33, -7.65) * mm, "end": v(22.65, -4.75) * mm});
            skLineSegment(sketch, "E36.5", {"start": v(22.65, -4.75) * mm, "end": v(24.33, -1.85) * mm});
            skPoint(sketch, "E36.0.midPoint", {"position": v(26, -1.85) * mm});
            skSolve(sketch);
        }
        {
            var Q0;
            Q0 = qSketchRegion(id + "F13", true);
            extrude(context, id + "F14", {"entities" : qUnion([Q0]), "operationType" : NewBodyOperationType.REMOVE, "oppositeDirection" : true, "depth" : 8 * mm});
        }
        {
            var Q0;
            Q0=makeQuery(id+"F7.opExtrude","SWEPT_FACE",FACE,{"disambiguationData":[OSD([sQuery(id+"F0.wireOp",EDGE,"E4.rect.bottom"),sQuery(id+"F4.wireOp",EDGE,"E10.bottom")])]});
            var sketch = newSketch(context, id + "F15", { "sketchPlane" : qUnion([Q0])});
            skLineSegment(sketch, "E37.0", {"start": v(19.35, 28) * mm, "end": v(19.35, 14) * mm});
            skLineSegment(sketch, "E38", {"start": v(19.35, 14) * mm, "end": v(19.35, 17.5) * mm, "construction": true});
            skLineSegment(sketch, "E39", {"start": v(19.35, 17.5) * mm, "end": v(15.85, 17.5) * mm, "construction": true});
            skCircle(sketch, "E40", {"center": v(15.85, 17.5) * mm, "radius": 3.5 * mm});
            skLineSegment(sketch, "E41", {"start": v(12.36, 17.62) * mm, "end": v(12.36, 14) * mm});
            skSolve(sketch);
        }
        {
            var Q0;
            {var subQ0=sQuery(id+"F15.wireOp",EDGE,"E41");var subQ1=sQuery(id+"F15.wireOp",EDGE,"E40");var subQ3=makeQuery(id+"F15.imprint","INTERSECT",VERTEX,{"disambiguationData":[OD(0.0)],"derivedFrom":[subQ1,subQ0]});Q0=makeQuery(id+"F15.imprint","IMPRINT",FACE,{"disambiguationData":[TD([[makeQuery(id+"F15.imprint","IMPRINT",EDGE,{"disambiguationData":[TD([[subQ3,1.0]])],"derivedFrom":subQ1}),1.0]])]});}
            var Q1;
            {var subQ1=sQuery(id+"F15.wireOp",EDGE,"E40");var subQ3=sQuery(id+"F15.wireOp",EDGE,"E41");var subQ5=makeQuery(id+"F15.imprint","INTERSECT",VERTEX,{"disambiguationData":[OD(1.0)],"derivedFrom":[subQ1,subQ3]});Q1=makeQuery(id+"F15.imprint","IMPRINT",FACE,{"disambiguationData":[TD([[makeQuery(id+"F15.imprint","IMPRINT",EDGE,{"disambiguationData":[TD([[subQ5,-1.0]])],"derivedFrom":subQ1}),-1.0]])]});}
            var Q2;
            {var subQ1=sQuery(id+"F15.wireOp",EDGE,"E40");var subQ3=sQuery(id+"F15.wireOp",EDGE,"E37.0");var subQ5=makeQuery(id+"F15.imprint","INTERSECT",VERTEX,{"derivedFrom":[subQ3,subQ1]});Q2=makeQuery(id+"F15.imprint","IMPRINT",FACE,{"disambiguationData":[TD([[makeQuery(id+"F15.imprint","IMPRINT",EDGE,{"disambiguationData":[TD([[subQ5,-1.0]])],"derivedFrom":subQ3}),-1.0]])]});}
            extrude(context, id + "F16", {"entities" : qUnion([Q0, Q1, Q2]), "operationType" : NewBodyOperationType.REMOVE, "oppositeDirection" : true, "depth" : 10 * mm});
        }
        {
            var Q0;
            Q0=makeQuery(id+"F7.opExtrude","CAP_EDGE",EDGE,{"disambiguationData":[OSD([sQuery(id+"F0.wireOp",EDGE,"E9")])],"isStart":false});
            var Q1;
            Q1=makeQuery(id+"F7.opExtrude","CAP_EDGE",EDGE,{"disambiguationData":[OSD([sQuery(id+"F0.wireOp",EDGE,"E8"),sQuery(id+"F4.wireOp",EDGE,"E10.top")])],"isStart":false});
            var Q2;
            Q2=makeQuery(id+"F7.opExtrude","CAP_EDGE",EDGE,{"disambiguationData":[OSD([sQuery(id+"F4.wireOp",EDGE,"E10.right")])],"isStart":false});
            var Q3;
            Q3=makeQuery(id+"F7.opExtrude","CAP_EDGE",EDGE,{"disambiguationData":[OSD([sQuery(id+"F0.wireOp",EDGE,"E4.rect.bottom"),sQuery(id+"F4.wireOp",EDGE,"E10.bottom")])],"isStart":false});
            var Q4;
            Q4=makeQuery(id+"F7.opExtrude","CAP_EDGE",EDGE,{"disambiguationData":[OSD([sQuery(id+"F0.wireOp",EDGE,"E4.rect.right")])],"isStart":false});
            var Q5;
            Q5=makeQuery(id+"F7.opExtrude","SWEPT_EDGE",EDGE,{"disambiguationData":[OSD([sQuery(id+"F0.wireOp",EDGE,"E4.rect.bottom"),sQuery(id+"F0.wireOp",EDGE,"E4.rect.right"),sQuery(id+"F4.wireOp",EDGE,"E10.bottom")])]});
            var Q6;
            {var subQ0=sQuery(id+"F0.wireOp",EDGE,"E4.rect.bottom");var subQ1=sQuery(id+"F0.wireOp",EDGE,"E4.rect.right");Q6=makeQuery(id+"F2.boolean.opBoolean","MERGE",EDGE,{"derivedFrom":[makeQuery(id+"F1.opExtrude","SWEPT_EDGE",EDGE,{"disambiguationData":[OSD([subQ0,subQ1])]}),makeQuery(id+"F2.opExtrude","SWEPT_EDGE",EDGE,{"disambiguationData":[OSD([subQ0,subQ1])]})]});}
            var Q7;
            {var subQ0=sQuery(id+"F0.wireOp",EDGE,"E4.rect.top");var subQ1=sQuery(id+"F0.wireOp",EDGE,"E4.rect.right");var subQ2=sQuery(id+"F0.wireOp",EDGE,"E9");Q7=makeQuery(id+"F2.boolean.opBoolean","MERGE",EDGE,{"derivedFrom":[makeQuery(id+"F1.opExtrude","SWEPT_EDGE",EDGE,{"disambiguationData":[OSD([subQ0,subQ1,subQ2])]}),makeQuery(id+"F2.opExtrude","SWEPT_EDGE",EDGE,{"disambiguationData":[OSD([subQ0,subQ1,subQ2])]})]});}
            var Q8;
            Q8=makeQuery(id+"F7.opExtrude","SWEPT_EDGE",EDGE,{"disambiguationData":[OSD([sQuery(id+"F0.wireOp",EDGE,"E4.rect.right"),sQuery(id+"F0.wireOp",EDGE,"E9")])]});
            var Q9;
            Q9=makeQuery(id+"F5.opExtrude","SWEPT_EDGE",EDGE,{"disambiguationData":[OSD([sQuery(id+"F4.wireOp",EDGE,"E10.top"),sQuery(id+"F4.wireOp",EDGE,"E10.right")])]});
            var Q10;
            Q10=makeQuery(id+"F7.opExtrude","SWEPT_EDGE",EDGE,{"disambiguationData":[OSD([sQuery(id+"F0.wireOp",EDGE,"E8"),sQuery(id+"F4.wireOp",EDGE,"E10.top"),sQuery(id+"F4.wireOp",EDGE,"E10.right")])]});
            var Q11;
            Q11=makeQuery(id+"F5.opExtrude","SWEPT_EDGE",EDGE,{"disambiguationData":[OSD([sQuery(id+"F4.wireOp",EDGE,"E10.bottom"),sQuery(id+"F4.wireOp",EDGE,"E10.right")])]});
            var Q12;
            Q12=makeQuery(id+"F7.opExtrude","SWEPT_EDGE",EDGE,{"disambiguationData":[OSD([sQuery(id+"F0.wireOp",EDGE,"E4.rect.bottom"),sQuery(id+"F4.wireOp",EDGE,"E10.bottom"),sQuery(id+"F4.wireOp",EDGE,"E10.right")])]});
            var Q13;
            Q13=makeQuery(id+"F5.opExtrude","CAP_EDGE",EDGE,{"disambiguationData":[OSD([sQuery(id+"F4.wireOp",EDGE,"E10.right")])],"isStart":true});
            var Q14;
            Q14=makeQuery(id+"F16.boolean.opBoolean","COPY",EDGE,{"derivedFrom":makeQuery(id+"F16.opExtrude","CAP_EDGE",EDGE,{"disambiguationData":[OSD([sQuery(id+"F15.wireOp",EDGE,"E40")])],"isStart":true})});
            var Q15;
            Q15=makeQuery(id+"F16.boolean.opBoolean","COPY",EDGE,{"derivedFrom":makeQuery(id+"F16.opExtrude","CAP_EDGE",EDGE,{"disambiguationData":[OSD([sQuery(id+"F15.wireOp",EDGE,"E41")])],"isStart":true})});
            fillet(context, id + "F17", {"entities" : qUnion([Q0, Q1, Q2, Q3, Q4, Q5, Q6, Q7, Q8, Q9, Q10, Q11, Q12, Q13, Q14, Q15]), "radius" : 1.5 * mm, "tangentPropagation" : true, "allowEdgeOverflow" : false});
        }
        {
            var Q0;
            Q0=makeQuery(id+"F16.boolean.opBoolean","INTERSECT",EDGE,{"derivedFrom":[makeQuery(id+"F9.boolean.opBoolean","COPY",FACE,{"derivedFrom":makeQuery(id+"F9.opExtrude","SWEPT_FACE",FACE,{"disambiguationData":[OSD([sQuery(id+"F8.wireOp",EDGE,"E14")])]})}),makeQuery(id+"F16.opExtrude","SWEPT_FACE",FACE,{"disambiguationData":[OSD([sQuery(id+"F15.wireOp",EDGE,"E40")])]})]});
            var Q1;
            Q1=makeQuery(id+"F16.boolean.opBoolean","INTERSECT",EDGE,{"derivedFrom":[makeQuery(id+"F9.boolean.opBoolean","COPY",FACE,{"derivedFrom":makeQuery(id+"F9.opExtrude","SWEPT_FACE",FACE,{"disambiguationData":[OSD([sQuery(id+"F8.wireOp",EDGE,"E14")])]})}),makeQuery(id+"F16.opExtrude","SWEPT_FACE",FACE,{"disambiguationData":[OSD([sQuery(id+"F15.wireOp",EDGE,"E41")])]})]});
            fillet(context, id + "F18", {"entities" : qUnion([Q0, Q1]), "radius" : 2 * mm, "tangentPropagation" : true, "allowEdgeOverflow" : false});
        }
    });
